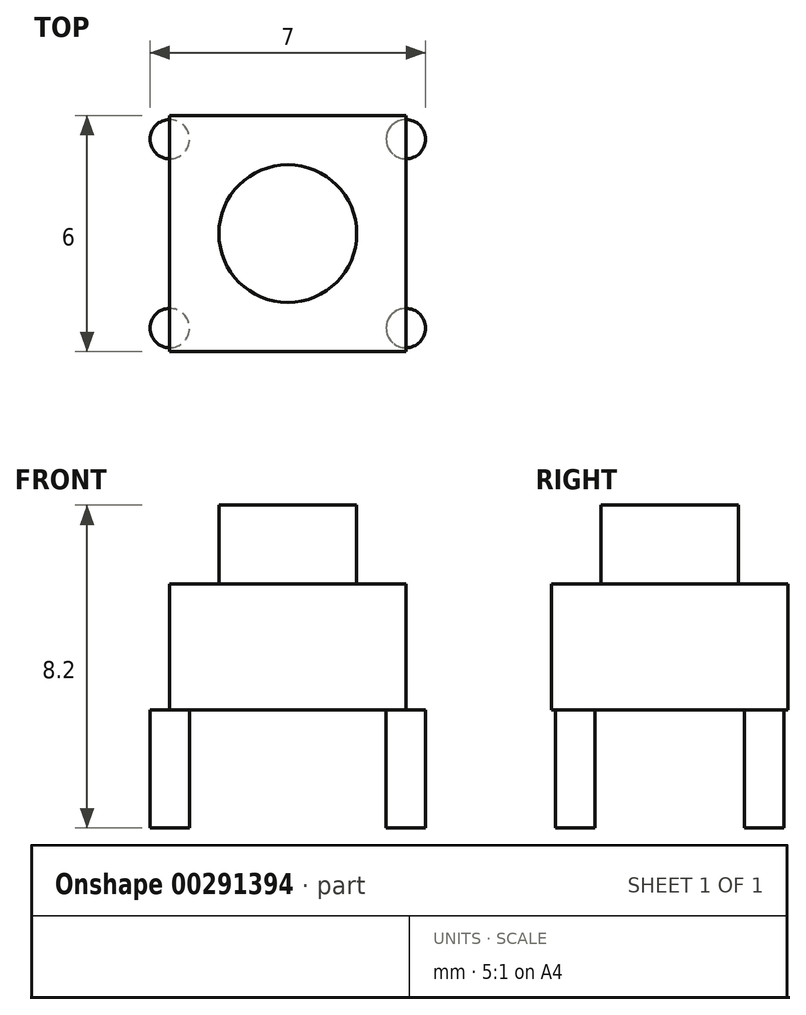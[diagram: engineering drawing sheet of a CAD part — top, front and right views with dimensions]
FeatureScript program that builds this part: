
annotation { "Feature Type Name" : "Feature", "Feature Type Description" : "" }
export const myFeature = defineFeature(function(context is Context, id is Id, definition is map)
    precondition{}
    {
        {
            var Q0;
            Q0=qCreatedBy(makeId("Top.planeOp"),FACE);
            var sketch = newSketch(context, id + "F0", { "sketchPlane" : qUnion([Q0])});
            skLineSegment(sketch, "E0.bottom", {"start": v(3, -3) * mm, "end": v(-3, -3) * mm});
            skLineSegment(sketch, "E0.top", {"start": v(3, 3) * mm, "end": v(-3, 3) * mm});
            skLineSegment(sketch, "E0.left", {"start": v(3, -3) * mm, "end": v(3, 3) * mm});
            skLineSegment(sketch, "E0.right", {"start": v(-3, -3) * mm, "end": v(-3, 3) * mm});
            skPoint(sketch, "E0.middle", {"position": v(0, 0) * mm});
            skSolve(sketch);
        }
        {
            var Q0;
            Q0 = qSketchRegion(id + "F0", true);
            extrude(context, id + "F1", {"entities" : qUnion([Q0]), "oppositeDirection" : true, "depth" : 3.2 * mm});
        }
        {
            var Q0;
            Q0=makeQuery(id+"F1.opExtrude","CAP_FACE",FACE,{"disambiguationData":[OSD([sQuery(id+"F0.wireOp",EDGE,"E0.bottom"),sQuery(id+"F0.wireOp",EDGE,"E0.top"),sQuery(id+"F0.wireOp",EDGE,"E0.left"),sQuery(id+"F0.wireOp",EDGE,"E0.right")])],"isStart":true});
            var sketch = newSketch(context, id + "F2", { "sketchPlane" : qUnion([Q0])});
            skCircle(sketch, "E1", {"center": v(0, 0) * mm, "radius": 1.75 * mm});
            skSolve(sketch);
        }
        {
            var Q0;
            Q0 = qSketchRegion(id + "F2", true);
            extrude(context, id + "F3", {"entities" : qUnion([Q0]), "operationType" : NewBodyOperationType.ADD, "depth" : 2 * mm});
        }
        {
            var Q0;
            Q0=makeQuery(id+"F1.opExtrude","CAP_FACE",FACE,{"disambiguationData":[OSD([sQuery(id+"F0.wireOp",EDGE,"E0.bottom"),sQuery(id+"F0.wireOp",EDGE,"E0.top"),sQuery(id+"F0.wireOp",EDGE,"E0.left"),sQuery(id+"F0.wireOp",EDGE,"E0.right")])],"isStart":false});
            var sketch = newSketch(context, id + "F4", { "sketchPlane" : qUnion([Q0])});
            skCircle(sketch, "E2", {"center": v(-3, 2.4) * mm, "radius": 0.5 * mm});
            skLineSegment(sketch, "E3", {"start": v(0, 3) * mm, "end": v(0, -3) * mm, "construction": true});
            skLineSegment(sketch, "E4", {"start": v(-3, 0) * mm, "end": v(3, 0) * mm, "construction": true});
            skCircle(sketch, "E5.MirrorC", {"center": v(3, 2.4) * mm, "radius": 0.5 * mm});
            skCircle(sketch, "E6.MirrorC", {"center": v(-3, -2.4) * mm, "radius": 0.5 * mm});
            skCircle(sketch, "E7.MirrorC", {"center": v(3, -2.4) * mm, "radius": 0.5 * mm});
            skSolve(sketch);
        }
        {
            var Q0;
            Q0 = qSketchRegion(id + "F4", true);
            extrude(context, id + "F5", {"entities" : qUnion([Q0]), "operationType" : NewBodyOperationType.ADD, "depth" : 3 * mm});
        }
    });
